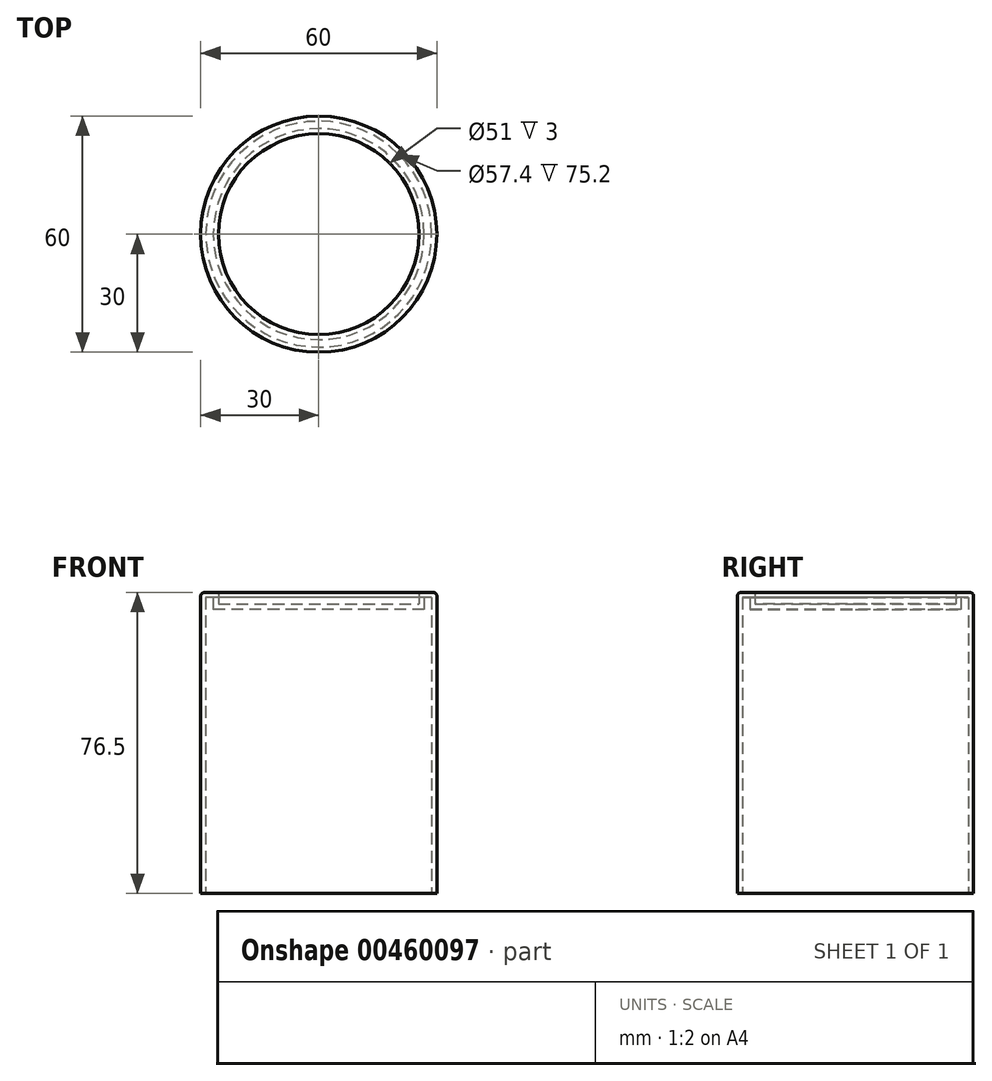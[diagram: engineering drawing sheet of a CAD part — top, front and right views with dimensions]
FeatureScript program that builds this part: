
annotation { "Feature Type Name" : "Feature", "Feature Type Description" : "" }
export const myFeature = defineFeature(function(context is Context, id is Id, definition is map)
    precondition{}
    {
        {
            var Q0;
            Q0=qCreatedBy(makeId("Top.planeOp"),FACE);
            var sketch = newSketch(context, id + "F0", { "sketchPlane" : qUnion([Q0])});
            skCircle(sketch, "E0", {"center": v(0, 0) * mm, "radius": 30 * mm});
            skSolve(sketch);
        }
        {
            var Q0;
            Q0=makeQuery(id+"F0.imprint","IMPRINT",FACE,{"disambiguationData":[TD([[makeQuery(id+"F0.imprint","IMPRINT",EDGE,{"derivedFrom":sQuery(id+"F0.wireOp",EDGE,"E0")}),1.0]])]});
            extrude(context, id + "F1", {"entities" : qUnion([Q0]), "depth" : 73 * mm});
        }
        {
            var Q0;
            Q0=makeQuery(id+"F1.opExtrude","CAP_FACE",FACE,{"disambiguationData":[OSD([sQuery(id+"F0.wireOp",EDGE,"E0")])],"isStart":false});
            extrude(context, id + "F2", {"entities" : qUnion([Q0]), "operationType" : NewBodyOperationType.ADD, "depth" : 3.5 * mm});
        }
        {
            var Q0;
            Q0=qCreatedBy(makeId("Top.planeOp"),FACE);
            cPlane(context, id + "F3", {"entities" : qUnion([Q0]), "cplaneType" : CPlaneType.OFFSET, "offset" : 73.5 * mm, "width" : 150 * mm, "height" : 150 * mm});
        }
        {
            var Q0;
            Q0=qCreatedBy(id+"F3.planeOp",FACE);
            var sketch = newSketch(context, id + "F4", { "sketchPlane" : qUnion([Q0])});
            skCircle(sketch, "E1", {"center": v(0, 0) * mm, "radius": 30 * mm});
            skSolve(sketch);
        }
        {
            var Q0;
            Q0=sQuery(id+"F4.wireOp",VERTEX,"E1.center");
            var Q1;
            Q1=makeQuery(id+"F1.opExtrude","SWEPT_BODY",BODY,{"disambiguationData":[OSD([sQuery(id+"F0.wireOp",EDGE,"E0")])]});
            hole(context, id + "F5", {"style" : HoleStyle.SIMPLE, "endStyle" : HoleEndStyle.BLIND, "oppositeDirection" : true, "holeDiameter" : 51 * mm, "holeDepth" : 3.5 * mm, "isTappedThrough" : true, "tappedDepth" : 12 * mm, "tapClearance" : 3, "locations" : qUnion([Q0]), "scope" : qUnion([Q1])});
        }
        {
            var Q0;
            Q0=makeQuery(id+"F2.opExtrude","CAP_EDGE",EDGE,{"disambiguationData":[OSD([sQuery(id+"F0.wireOp",EDGE,"E0")])],"isStart":false});
            var Q1;
            Q1=makeQuery(id+"F5.hole-0.boolean.opBoolean","INTERSECT",EDGE,{"derivedFrom":[makeQuery(id+"F2.opExtrude","CAP_FACE",FACE,{"disambiguationData":[OSD([sQuery(id+"F0.wireOp",EDGE,"E0")])],"isStart":false}),makeQuery(id+"F5.hole-0.opRevolve","SWEPT_FACE",FACE,{"disambiguationData":[OSD([sQuery(id+"F5.hole-0.sketch.wireOp",EDGE,"core_line_2")])]})]});
            fillet(context, id + "F6", {"entities" : qUnion([Q0, Q1]), "radius" : 1 * mm, "tangentPropagation" : true, "allowEdgeOverflow" : false});
        }
        {
            var Q0;
            Q0=makeQuery(id+"F1.opExtrude","CAP_FACE",FACE,{"disambiguationData":[OSD([sQuery(id+"F0.wireOp",EDGE,"E0")])],"isStart":true});
            shell(context, id + "F7", {"entities" : qUnion([Q0]), "thickness" : 1.3 * mm});
        }
    });
